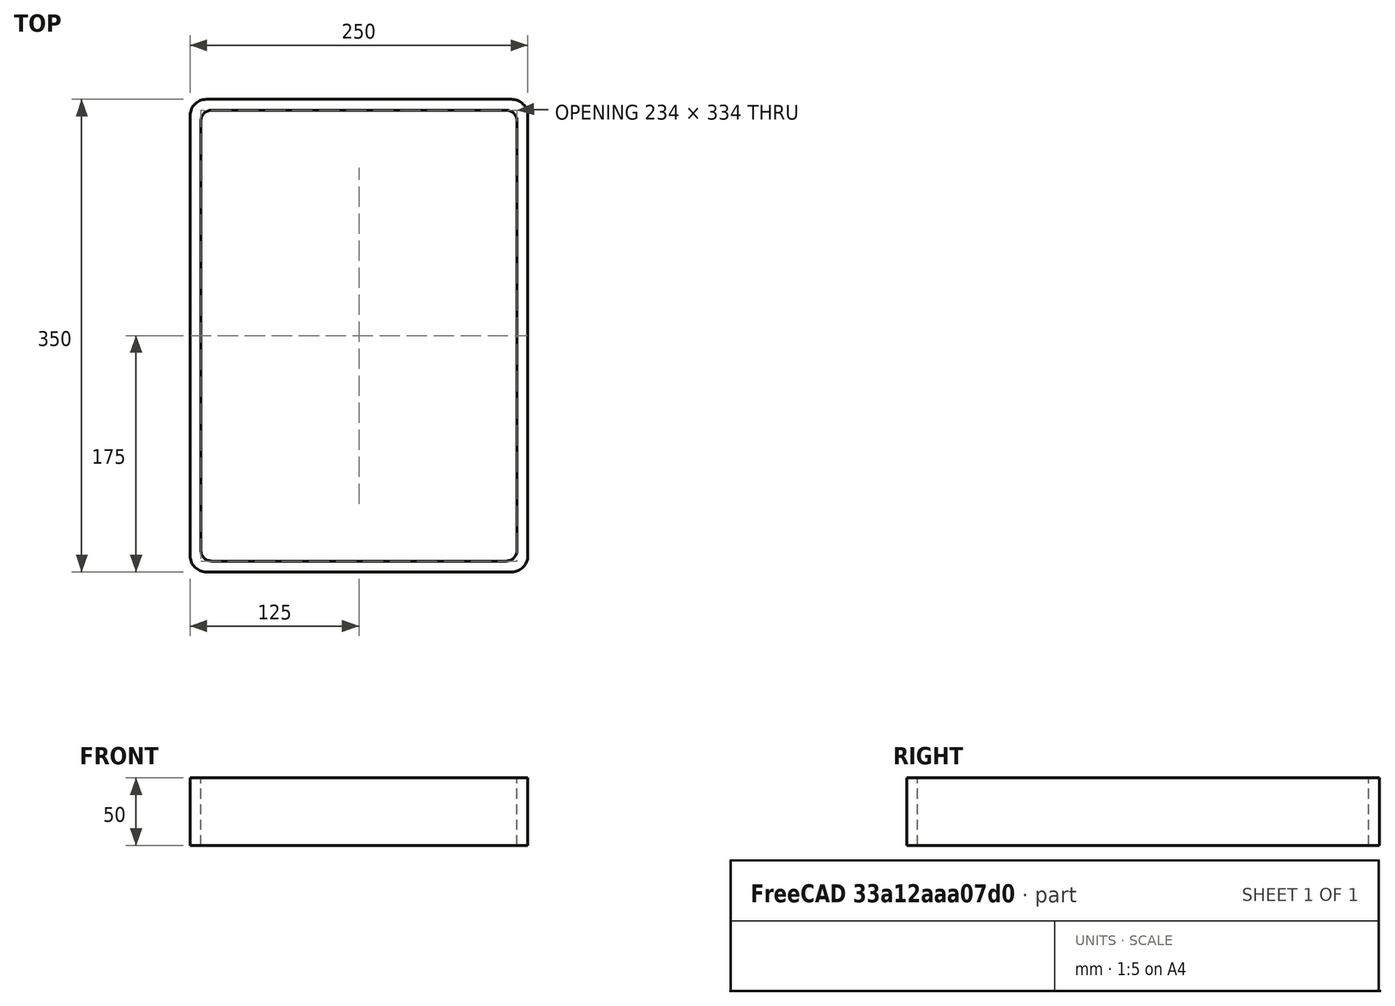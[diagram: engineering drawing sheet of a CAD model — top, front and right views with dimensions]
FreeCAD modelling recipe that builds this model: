
FCSTD DOCUMENT  (FreeCAD 0.15R4671 (Git))
Label: Rectangular hollow section 350x250x8 EN10219 S235JRH
License: All rights reserved
LicenseURL: http://en.wikipedia.org/wiki/All_rights_reserved
objects: Sketcher::SketchObject×1, Part::Extrusion×1
note: 2 computed .brp shape members not serialized (recipe doc carries the construction recipe); baked Part::Feature solids carry a one-line shape summary decoded from their .brp

FEATURE [Sketcher::SketchObject] Sketch
  sketch-geometry (16):
    g0: LineSegment StartX=-109 StartY=167 StartZ=0 EndX=109 EndY=167 EndZ=0
    g1: LineSegment StartX=117 StartY=159 StartZ=0 EndX=117 EndY=-159 EndZ=0
    g2: LineSegment StartX=109 StartY=-167 StartZ=0 EndX=-109 EndY=-167 EndZ=0
    g3: LineSegment StartX=-117 StartY=-159 StartZ=0 EndX=-117 EndY=159 EndZ=0
    g4: LineSegment StartX=-113 StartY=175 StartZ=0 EndX=113 EndY=175 EndZ=0
    g5: LineSegment StartX=125 StartY=163 StartZ=0 EndX=125 EndY=-163 EndZ=0
    g6: LineSegment StartX=113 StartY=-175 StartZ=0 EndX=-113 EndY=-175 EndZ=0
    g7: LineSegment StartX=-125 StartY=-163 StartZ=0 EndX=-125 EndY=163 EndZ=0
    g8: ArcOfCircle CenterX=-109 CenterY=159 CenterZ=0 NormalX=0 NormalY=0 NormalZ=1 Radius=8 StartAngle=1.5708 EndAngle=3.14159
    g9: ArcOfCircle CenterX=109 CenterY=159 CenterZ=0 NormalX=0 NormalY=0 NormalZ=1 Radius=8 StartAngle=0 EndAngle=1.5708
    g10: ArcOfCircle CenterX=109 CenterY=-159 CenterZ=0 NormalX=0 NormalY=0 NormalZ=1 Radius=8 StartAngle=4.71239 EndAngle=6.28319
    g11: ArcOfCircle CenterX=-109 CenterY=-159 CenterZ=0 NormalX=0 NormalY=0 NormalZ=1 Radius=8 StartAngle=3.14159 EndAngle=4.71239
    g12: ArcOfCircle CenterX=113 CenterY=163 CenterZ=0 NormalX=0 NormalY=0 NormalZ=1 Radius=12 StartAngle=0 EndAngle=1.5708
    g13: ArcOfCircle CenterX=113 CenterY=-163 CenterZ=0 NormalX=0 NormalY=0 NormalZ=1 Radius=12 StartAngle=4.71239 EndAngle=6.28319
    g14: ArcOfCircle CenterX=-113 CenterY=-163 CenterZ=0 NormalX=0 NormalY=0 NormalZ=1 Radius=12 StartAngle=3.14159 EndAngle=4.71239
    g15: ArcOfCircle CenterX=-113 CenterY=163 CenterZ=0 NormalX=0 NormalY=0 NormalZ=1 Radius=12 StartAngle=1.5708 EndAngle=3.14159
  constraints (36):
    c: Horizontal(g2)
    c: Vertical(g3)
    c: Horizontal(g6)
    c: Vertical(g7)
    c: Tangent(g3,g8) = 1.5708
    c: Tangent(g0,g8) = 1.5708
    c: Tangent(g0,g9) = 1.5708
    c: Tangent(g1,g9) = 1.5708
    c: Tangent(g1,g10) = 1.5708
    c: Tangent(g2,g10) = 1.5708
    c: Tangent(g2,g11) = 1.5708
    c: Tangent(g3,g11) = 1.5708
    c: Tangent(g4,g12) = 1.5708
    c: Tangent(g5,g12) = 1.5708
    c: Tangent(g5,g13) = 1.5708
    c: Tangent(g6,g13) = 1.5708
    c: Tangent(g6,g14) = 1.5708
    c: Tangent(g7,g14) = 1.5708
    c: Tangent(g7,g15) = 1.5708
    c: Tangent(g4,g15) = 1.5708
    c: Equal(g9,g8)
    c: Equal(g9,g11)
    c: Equal(g9,g10)
    c: Equal(g12,g15)
    c: Equal(g12,g14)
    c: Equal(g12,g13)
    c: Symmetric(g4,g6,g-1)
    c: Symmetric(g7,g5,g-2)
    c: DistanceY(g4,g6) = -350
    c: DistanceX(g7,g5) = 250
    c: Symmetric(g3,g1,g-2)
    c: Symmetric(g0,g2,g-1)
    c: DistanceY(g0,g4) = 8
    c: DistanceX(g5,g1) = -8
    c: Radius(g9) = 8
    c: Radius(g12) = 12
FEATURE [Part::Extrusion] Extrude  label="Rectangular hollow section 350x250x8 EN10219 S235JRH"
  Base = -> Sketch
  Dir = (0,0,50)
  Solid = true
